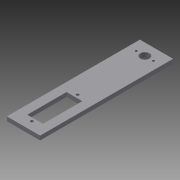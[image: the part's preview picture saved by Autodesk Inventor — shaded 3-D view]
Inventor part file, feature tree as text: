
AUTODESK INVENTOR PART (.ipt)
format: ipt  version: 2013 (Build 170138000, 138)  size: 98,816 bytes
history: native  units: in
note: dims shown in document units (in); Inventor stores cm internally (conversion verified against a paired STEP export)
features: extrude x1, sketch x1
ambient origin geometry x8: Origin, YZ Plane, XZ Plane, XY Plane, X Axis, Y Axis, Z Axis, Center Point
bodies: Solid1 (feature_tree)
feature tree (2):
  extrude  "Extrusion1"  Depth=4.0in
  sketch  "Sketch1"  dims[d0=1.0in d1=4.0in d2=0.276in d3=0.35in d4=0.5in d5=0.07in d6=0.07in d7=0.518in d8=0.259in d9=0.35in d10=0.35in d11=0.4724in d12=1.1811in d13=0.35in d14=0.2638in d15=0.083in d16=0.083in d17=0.2362in d18=0.2362in d19=1.378in d20=0.0984in d21=0.125in d22=0.0in]
